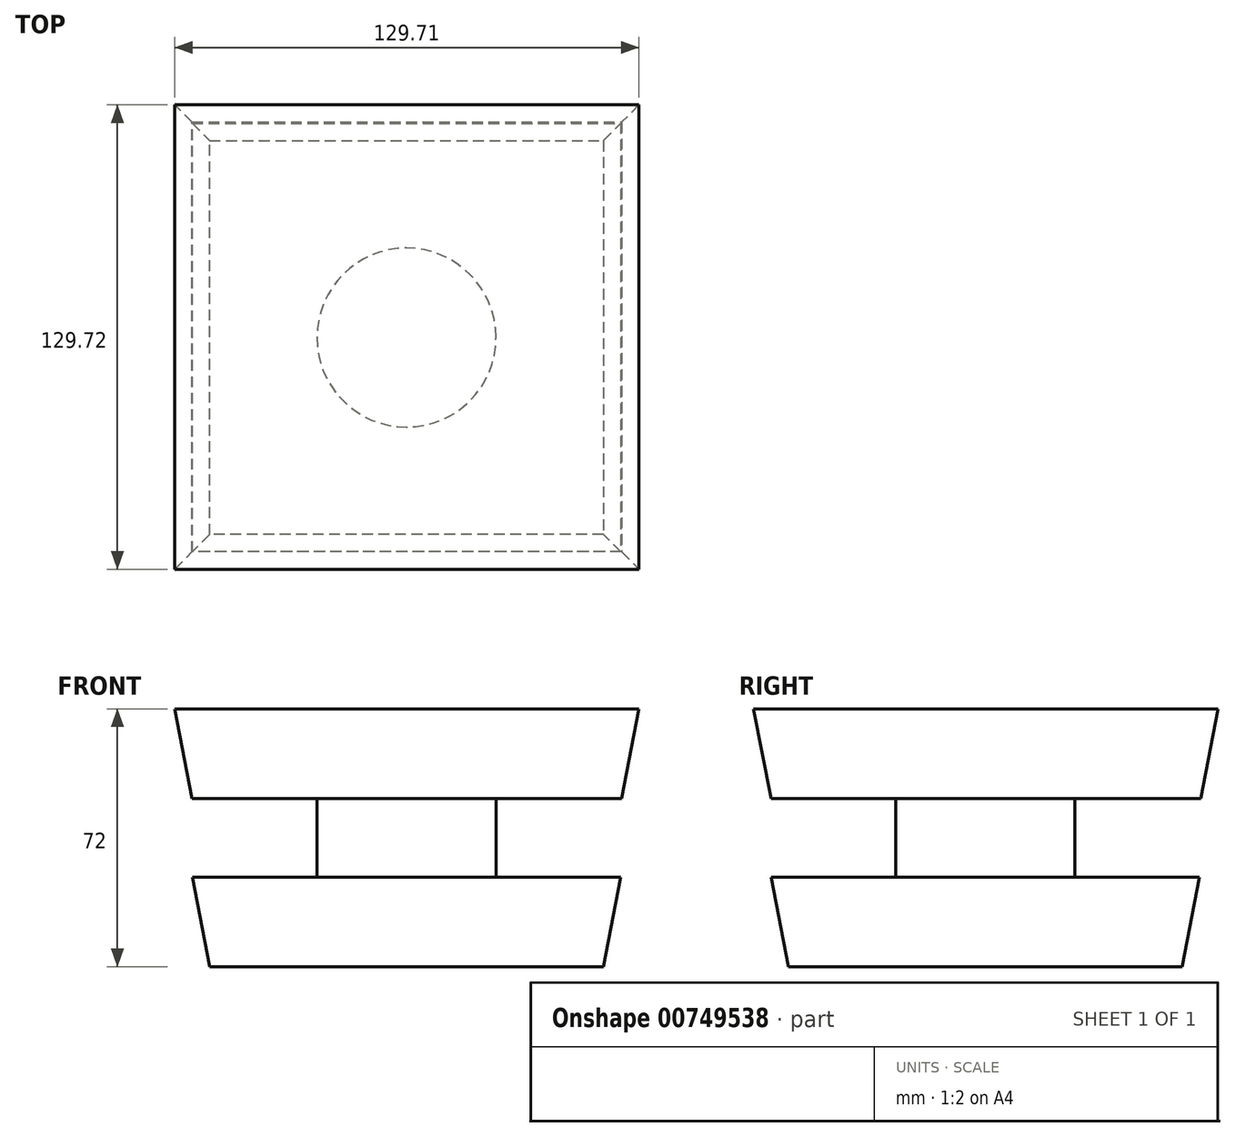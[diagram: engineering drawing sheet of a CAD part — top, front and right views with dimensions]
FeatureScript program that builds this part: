
annotation { "Feature Type Name" : "Feature", "Feature Type Description" : "" }
export const myFeature = defineFeature(function(context is Context, id is Id, definition is map)
    precondition{}
    {
        {
            var Q0;
            Q0=qCreatedBy(makeId("Top.planeOp"),FACE);
            var sketch = newSketch(context, id + "F0", { "sketchPlane" : qUnion([Q0])});
            skLineSegment(sketch, "E0.bottom", {"start": v(0, 0) * mm, "end": v(110, 0) * mm});
            skLineSegment(sketch, "E0.top", {"start": v(0, 110) * mm, "end": v(110, 110) * mm});
            skLineSegment(sketch, "E0.left", {"start": v(0, 0) * mm, "end": v(0, 110) * mm});
            skLineSegment(sketch, "E0.right", {"start": v(110, 0) * mm, "end": v(110, 110) * mm});
            skSolve(sketch);
        }
        {
            var Q0;
            Q0 = qSketchRegion(id + "F0", true);
            extrude(context, id + "F1", {"entities" : qUnion([Q0]), "depth" : 25 * mm, "offsetDistance" : 25 * mm, "hasDraft" : true, "draftAngle" : 11 * degree});
        }
        {
            var Q0;
            Q0=makeQuery(id+"F1.opExtrude","CAP_FACE",FACE,{"disambiguationData":[OSD([sQuery(id+"F0.wireOp",EDGE,"E0.bottom"),sQuery(id+"F0.wireOp",EDGE,"E0.top"),sQuery(id+"F0.wireOp",EDGE,"E0.left"),sQuery(id+"F0.wireOp",EDGE,"E0.right")])],"isStart":false});
            var sketch = newSketch(context, id + "F2", { "sketchPlane" : qUnion([Q0])});
            skCircle(sketch, "E1", {"center": v(55, 55) * mm, "radius": 25 * mm});
            skPoint(sketch, "E1.centerSnap0", {"position": v(-4.86, 55) * mm});
            skPoint(sketch, "E1.centerSnap1", {"position": v(55, -4.86) * mm});
            skSolve(sketch);
        }
        {
            var Q0;
            Q0 = qSketchRegion(id + "F2", true);
            var Q1;
            Q1=makeQuery(id+"F2.imprint","IMPRINT",FACE,{"disambiguationData":[TD([[makeQuery(id+"F2.imprint","IMPRINT",EDGE,{"derivedFrom":sQuery(id+"F2.wireOp",EDGE,"E1")}),1.0]])]});
            extrude(context, id + "F3", {"entities" : qUnion([Q0, Q1]), "operationType" : NewBodyOperationType.ADD, "depth" : 22 * mm, "offsetDistance" : 25 * mm});
        }
        {
            var Q0;
            Q0=makeQuery(id+"F3.opExtrude","CAP_FACE",FACE,{"disambiguationData":[OSD([sQuery(id+"F2.wireOp",EDGE,"E1")])],"isStart":false});
            var sketch = newSketch(context, id + "F4", { "sketchPlane" : qUnion([Q0])});
            skLineSegment(sketch, "E2.bottom", {"start": v(-4.89, 115.16) * mm, "end": v(115.11, 115.16) * mm});
            skLineSegment(sketch, "E2.top", {"start": v(-4.89, -4.84) * mm, "end": v(115.11, -4.84) * mm});
            skLineSegment(sketch, "E2.left", {"start": v(-4.89, 115.16) * mm, "end": v(-4.89, -4.84) * mm});
            skLineSegment(sketch, "E2.right", {"start": v(115.11, 115.16) * mm, "end": v(115.11, -4.84) * mm});
            skSolve(sketch);
        }
        {
            var Q0;
            Q0=makeQuery(id+"F4.imprint","IMPRINT",FACE,{"disambiguationData":[TD([[makeQuery(id+"F4.imprint","IMPRINT",EDGE,{"derivedFrom":makeQuery(id+"F3.opExtrude","CAP_EDGE",EDGE,{"disambiguationData":[OSD([sQuery(id+"F2.wireOp",EDGE,"E1")])],"isStart":false})}),1.0]])]});
            var Q1;
            Q1=makeQuery(id+"F4.imprint","IMPRINT",FACE,{"disambiguationData":[TD([[makeQuery(id+"F4.imprint","IMPRINT",EDGE,{"derivedFrom":sQuery(id+"F4.wireOp",EDGE,"E2.bottom")}),-1.0]])]});
            extrude(context, id + "F5", {"entities" : qUnion([Q0, Q1]), "operationType" : NewBodyOperationType.ADD, "depth" : 25 * mm, "offsetDistance" : 25 * mm, "hasDraft" : true, "draftAngle" : 11 * degree});
        }
    });
